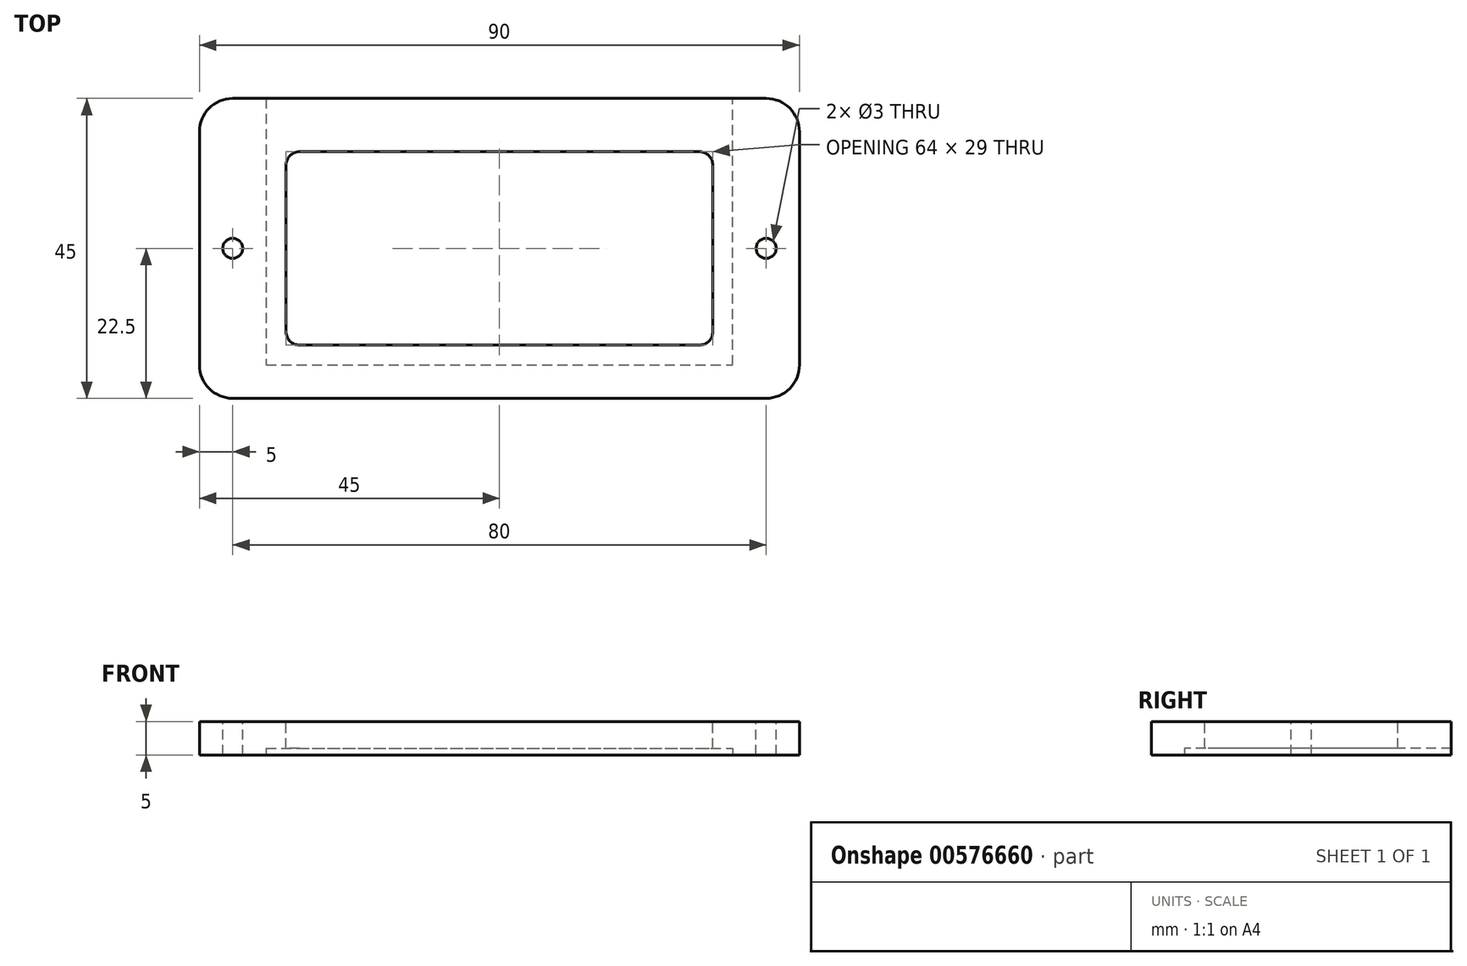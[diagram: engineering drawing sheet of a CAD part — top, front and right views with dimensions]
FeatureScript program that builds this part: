
annotation { "Feature Type Name" : "Feature", "Feature Type Description" : "" }
export const myFeature = defineFeature(function(context is Context, id is Id, definition is map)
    precondition{}
    {
        {
            var Q0;
            Q0=qCreatedBy(makeId("Top.planeOp"),FACE);
            var sketch = newSketch(context, id + "F0", { "sketchPlane" : qUnion([Q0])});
            skLineSegment(sketch, "E0.bottom", {"start": v(0, 0) * mm, "end": v(90, 0) * mm});
            skLineSegment(sketch, "E0.top", {"start": v(0, 45) * mm, "end": v(90, 45) * mm});
            skLineSegment(sketch, "E0.left", {"start": v(0, 0) * mm, "end": v(0, 45) * mm});
            skLineSegment(sketch, "E0.right", {"start": v(90, 0) * mm, "end": v(90, 45) * mm});
            skSolve(sketch);
        }
        {
            var Q0;
            Q0=qSketchRegion(id+"F0",true);
            extrude(context, id + "F1", {"entities" : qUnion([Q0]), "depth" : 5 * mm});
        }
        {
            var Q0;
            Q0=makeQuery(id+"F1.opExtrude","SWEPT_EDGE",EDGE,{"disambiguationData":[OSD([sQuery(id+"F0.wireOp",EDGE,"E0.top"),sQuery(id+"F0.wireOp",EDGE,"E0.right")])]});
            var Q1;
            Q1=makeQuery(id+"F1.opExtrude","SWEPT_EDGE",EDGE,{"disambiguationData":[OSD([sQuery(id+"F0.wireOp",EDGE,"E0.bottom"),sQuery(id+"F0.wireOp",EDGE,"E0.right")])]});
            var Q2;
            Q2=makeQuery(id+"F1.opExtrude","SWEPT_EDGE",EDGE,{"disambiguationData":[OSD([sQuery(id+"F0.wireOp",EDGE,"E0.top"),sQuery(id+"F0.wireOp",EDGE,"E0.left")])]});
            var Q3;
            Q3=makeQuery(id+"F1.opExtrude","SWEPT_EDGE",EDGE,{"disambiguationData":[OSD([sQuery(id+"F0.wireOp",EDGE,"E0.bottom"),sQuery(id+"F0.wireOp",EDGE,"E0.left")])]});
            fillet(context, id + "F2", {"entities" : qUnion([Q0, Q1, Q2, Q3]), "radius" : 5 * mm, "tangentPropagation" : true, "allowEdgeOverflow" : false});
        }
        {
            var Q0;
            Q0=qCreatedBy(makeId("Top.planeOp"),FACE);
            var sketch = newSketch(context, id + "F3", { "sketchPlane" : qUnion([Q0])});
            skLineSegment(sketch, "E1", {"start": v(10, 45) * mm, "end": v(10, 5) * mm});
            skLineSegment(sketch, "E2", {"start": v(10, 5) * mm, "end": v(80, 5) * mm});
            skLineSegment(sketch, "E3", {"start": v(80, 5) * mm, "end": v(80, 45) * mm});
            skLineSegment(sketch, "E4.0", {"start": v(10, 45) * mm, "end": v(80, 45) * mm});
            skPoint(sketch, "E5.orphan", {"position": v(5, 45) * mm});
            skPoint(sketch, "E6.orphan", {"position": v(85, 45) * mm});
            skPoint(sketch, "E7.orphan", {"position": v(99.44, 5) * mm});
            skSolve(sketch);
        }
        {
            var Q0;
            Q0=qSketchRegion(id+"F3",true);
            extrude(context, id + "F4", {"entities" : qUnion([Q0]), "operationType" : NewBodyOperationType.REMOVE, "depth" : 1 * mm});
        }
        {
            var Q0;
            Q0=makeQuery(id+"F1.opExtrude","CAP_FACE",FACE,{"disambiguationData":[OSD([sQuery(id+"F0.wireOp",EDGE,"E0.bottom"),sQuery(id+"F0.wireOp",EDGE,"E0.top"),sQuery(id+"F0.wireOp",EDGE,"E0.left"),sQuery(id+"F0.wireOp",EDGE,"E0.right")])],"isStart":false});
            var sketch = newSketch(context, id + "F5", { "sketchPlane" : qUnion([Q0])});
            skLineSegment(sketch, "E8.bottom", {"start": v(15, 37) * mm, "end": v(75, 37) * mm});
            skLineSegment(sketch, "E8.top", {"start": v(15, 8) * mm, "end": v(75, 8) * mm});
            skLineSegment(sketch, "E8.left", {"start": v(13, 35) * mm, "end": v(13, 10) * mm});
            skLineSegment(sketch, "E8.right", {"start": v(77, 35) * mm, "end": v(77, 10) * mm});
            skPoint(sketch, "E9.visualSharp", {"position": v(13, 37) * mm});
            skArc(sketch, "E9.filletArc", {"start": v(15, 37) * mm, "mid": v(13.59, 36.41) * mm, "end": v(13, 35) * mm});
            skPoint(sketch, "E10.visualSharp", {"position": v(13, 8) * mm});
            skArc(sketch, "E10.filletArc", {"start": v(13, 10) * mm, "mid": v(13.59, 8.59) * mm, "end": v(15, 8) * mm});
            skPoint(sketch, "E11.visualSharp", {"position": v(77, 8) * mm});
            skArc(sketch, "E11.filletArc", {"start": v(75, 8) * mm, "mid": v(76.41, 8.59) * mm, "end": v(77, 10) * mm});
            skPoint(sketch, "E12.visualSharp", {"position": v(77, 37) * mm});
            skArc(sketch, "E12.filletArc", {"start": v(77, 35) * mm, "mid": v(76.41, 36.41) * mm, "end": v(75, 37) * mm});
            skSolve(sketch);
        }
        {
            var Q0;
            Q0=qSketchRegion(id+"F5",true);
            extrude(context, id + "F6", {"entities" : qUnion([Q0]), "operationType" : NewBodyOperationType.REMOVE, "oppositeDirection" : true, "depth" : 25 * mm});
        }
        {
            var Q0;
            Q0=makeQuery(id+"F1.opExtrude","CAP_FACE",FACE,{"disambiguationData":[OSD([sQuery(id+"F0.wireOp",EDGE,"E0.bottom"),sQuery(id+"F0.wireOp",EDGE,"E0.top"),sQuery(id+"F0.wireOp",EDGE,"E0.left"),sQuery(id+"F0.wireOp",EDGE,"E0.right")])],"isStart":false});
            var sketch = newSketch(context, id + "F7", { "sketchPlane" : qUnion([Q0])});
            skLineSegment(sketch, "E13", {"start": v(0, 22.5) * mm, "end": v(5, 22.5) * mm, "construction": true});
            skLineSegment(sketch, "E14", {"start": v(90, 22.5) * mm, "end": v(85, 22.5) * mm, "construction": true});
            skCircle(sketch, "E15", {"center": v(5, 22.5) * mm, "radius": 1.5 * mm});
            skCircle(sketch, "E16", {"center": v(85, 22.5) * mm, "radius": 1.5 * mm});
            skSolve(sketch);
        }
        {
            var Q0;
            Q0=qSketchRegion(id+"F7",true);
            extrude(context, id + "F8", {"entities" : qUnion([Q0]), "operationType" : NewBodyOperationType.REMOVE, "oppositeDirection" : true, "depth" : 25 * mm});
        }
    });
